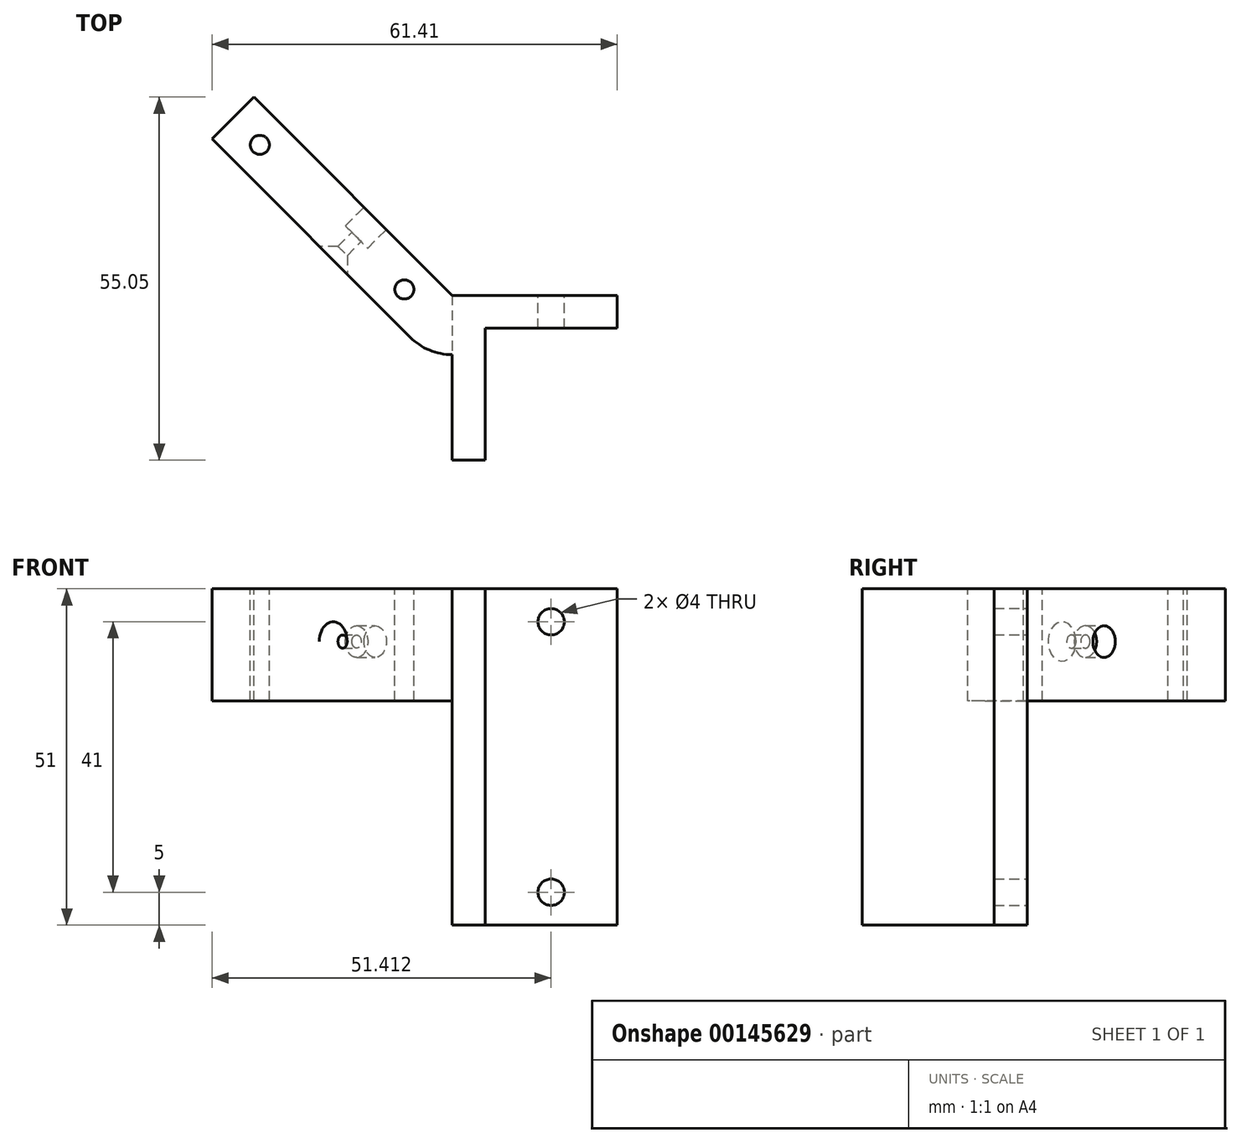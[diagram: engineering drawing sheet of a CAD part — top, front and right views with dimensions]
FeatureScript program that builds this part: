
annotation { "Feature Type Name" : "Feature", "Feature Type Description" : "" }
export const myFeature = defineFeature(function(context is Context, id is Id, definition is map)
    precondition{}
    {
        {
            var Q0;
            Q0=qCreatedBy(makeId("Top.planeOp"),FACE);
            var sketch = newSketch(context, id + "F0", { "sketchPlane" : qUnion([Q0])});
            skLineSegment(sketch, "E0", {"start": v(0.11, 9.4) * mm, "end": v(0.11, 0.4) * mm});
            skLineSegment(sketch, "E1", {"start": v(0.11, 0.4) * mm, "end": v(0.11, -15.6) * mm});
            skLineSegment(sketch, "E2", {"start": v(0.11, -15.6) * mm, "end": v(5.11, -15.6) * mm});
            skLineSegment(sketch, "E3", {"start": v(5.11, -15.6) * mm, "end": v(5.11, 4.4) * mm});
            skLineSegment(sketch, "E4", {"start": v(5.11, 4.4) * mm, "end": v(25.11, 4.4) * mm});
            skLineSegment(sketch, "E5", {"start": v(25.11, 9.4) * mm, "end": v(0.11, 9.4) * mm});
            skLineSegment(sketch, "E6", {"start": v(-29.94, 39.46) * mm, "end": v(0.11, 9.4) * mm});
            skLineSegment(sketch, "E7", {"start": v(0.11, 9.4) * mm, "end": v(-6.25, 3.04) * mm});
            skLineSegment(sketch, "E8", {"start": v(-6.25, 3.04) * mm, "end": v(-36.3, 33.1) * mm});
            skLineSegment(sketch, "E9", {"start": v(-36.3, 33.1) * mm, "end": v(-29.94, 39.46) * mm});
            skLineSegment(sketch, "E10", {"start": v(-33.12, 36.28) * mm, "end": v(-29.06, 32.2) * mm, "construction": true});
            skLineSegment(sketch, "E11", {"start": v(-29.06, 32.2) * mm, "end": v(-7.14, 10.29) * mm, "construction": true});
            skLineSegment(sketch, "E12", {"start": v(-7.14, 10.29) * mm, "end": v(-3.07, 6.22) * mm, "construction": true});
            skCircle(sketch, "E13", {"center": v(-29.06, 32.2) * mm, "radius": 1.45 * mm});
            skCircle(sketch, "E14", {"center": v(-7.14, 10.29) * mm, "radius": 1.45 * mm});
            skCircle(sketch, "E15", {"center": v(0.11, 9.4) * mm, "radius": 9 * mm});
            skLineSegment(sketch, "E16", {"start": v(25.11, 9.4) * mm, "end": v(25.11, 4.4) * mm});
            skSolve(sketch);
        }
        {
            var Q0;
            {var subQ1=sQuery(id+"F0.wireOp",EDGE,"E8");Q0=makeQuery(id+"F0.imprint","IMPRINT",FACE,{"disambiguationData":[TD([[makeQuery(id+"F0.imprint","IMPRINT",EDGE,{"derivedFrom":subQ1}),-1.0]])]});}
            var Q1;
            {var subQ0=sQuery(id+"F0.wireOp",EDGE,"E7");Q1=makeQuery(id+"F0.imprint","IMPRINT",FACE,{"disambiguationData":[TD([[makeQuery(id+"F0.imprint","IMPRINT",EDGE,{"derivedFrom":subQ0}),-1.0]])]});}
            var Q2;
            {var subQ0=sQuery(id+"F0.wireOp",EDGE,"E0");Q2=makeQuery(id+"F0.imprint","IMPRINT",FACE,{"disambiguationData":[TD([[makeQuery(id+"F0.imprint","IMPRINT",EDGE,{"derivedFrom":subQ0}),-1.0]])]});}
            var Q3;
            {var subQ4=sQuery(id+"F0.wireOp",EDGE,"kEGB38dB-wI6o-vp5B-2OdH-hbcTewE5rvnv");Q3=makeQuery(id+"F0.imprint","IMPRINT",FACE,{"disambiguationData":[TD([[makeQuery(id+"F0.imprint","IMPRINT",EDGE,{"derivedFrom":subQ4}),1.0]])]});}
            extrude(context, id + "F1", {"entities" : qUnion([Q0, Q1, Q2, Q3]), "oppositeDirection" : true, "depth" : 17 * mm});
        }
        {
            var Q0;
            {var subQ0=sQuery(id+"F0.wireOp",EDGE,"E1");Q0=makeQuery(id+"F0.imprint","IMPRINT",FACE,{"disambiguationData":[TD([[makeQuery(id+"F0.imprint","IMPRINT",EDGE,{"derivedFrom":subQ0}),1.0]])]});}
            var Q1;
            {var subQ1=sQuery(id+"F0.wireOp",EDGE,"E0");Q1=makeQuery(id+"F0.imprint","IMPRINT",FACE,{"disambiguationData":[TD([[makeQuery(id+"F0.imprint","IMPRINT",EDGE,{"derivedFrom":subQ1}),1.0]])]});}
            var Q2;
            {var subQ4=sQuery(id+"F0.wireOp",EDGE,"kEGB38dB-wI6o-vp5B-2OdH-hbcTewE5rvnv");Q2=makeQuery(id+"F0.imprint","IMPRINT",FACE,{"disambiguationData":[TD([[makeQuery(id+"F0.imprint","IMPRINT",EDGE,{"derivedFrom":subQ4}),1.0]])]});}
            var Q3;
            {var subQ0=sQuery(id+"F0.wireOp",EDGE,"E16");Q3=makeQuery(id+"F0.imprint","IMPRINT",FACE,{"disambiguationData":[TD([[makeQuery(id+"F0.imprint","IMPRINT",EDGE,{"derivedFrom":subQ0}),-1.0]])]});}
            extrude(context, id + "F2", {"entities" : qUnion([Q0, Q1, Q2, Q3]), "operationType" : NewBodyOperationType.ADD, "oppositeDirection" : true, "depth" : (17 + 34) * mm});
        }
        {
            var Q0;
            Q0=makeQuery(id+"F1.opExtrude","SWEPT_FACE",FACE,{"disambiguationData":[OSD([sQuery(id+"F0.wireOp",EDGE,"E6")])]});
            var sketch = newSketch(context, id + "F3", { "sketchPlane" : qUnion([Q0])});
            skLineSegment(sketch, "E17", {"start": v(23.07, 0) * mm, "end": v(23.07, -17) * mm, "construction": true});
            skLineSegment(sketch, "E18", {"start": v(49.07, -8) * mm, "end": v(6.57, -8) * mm, "construction": true});
            skPoint(sketch, "E19", {"position": v(23.07, -8) * mm});
            skCircle(sketch, "E20", {"center": v(23.07, -8) * mm, "radius": 2.4 * mm});
            skCircle(sketch, "E21", {"center": v(23.07, -8) * mm, "radius": 1 * mm});
            skSolve(sketch);
        }
        {
            var Q0;
            Q0=makeQuery(id+"F3.imprint","IMPRINT",FACE,{"disambiguationData":[TD([[makeQuery(id+"F3.imprint","IMPRINT",EDGE,{"derivedFrom":sQuery(id+"F3.wireOp",EDGE,"E21")}),1.0]])]});
            extrude(context, id + "F4", {"entities" : qUnion([Q0]), "operationType" : NewBodyOperationType.REMOVE, "endBound" : BoundingType.THROUGH_ALL, "oppositeDirection" : true, "depth" : 25 * mm});
        }
        {
            var Q0;
            Q0=makeQuery(id+"F3.imprint","IMPRINT",FACE,{"disambiguationData":[TD([[makeQuery(id+"F3.imprint","IMPRINT",EDGE,{"derivedFrom":sQuery(id+"F3.wireOp",EDGE,"E20")}),1.0]])]});
            extrude(context, id + "F5", {"entities" : qUnion([Q0]), "operationType" : NewBodyOperationType.REMOVE, "oppositeDirection" : true, "depth" : 4 * mm});
        }
        {
            var Q0;
            Q0=makeQuery(id+"F4.boolean.opBoolean","INTERSECT",EDGE,{"derivedFrom":[makeQuery(id+"F1.opExtrude","SWEPT_FACE",FACE,{"disambiguationData":[OSD([sQuery(id+"F0.wireOp",EDGE,"E8")])]}),makeQuery(id+"F4.opExtrude","SWEPT_FACE",FACE,{"disambiguationData":[OSD([sQuery(id+"F3.wireOp",EDGE,"E21")])]})]});
            chamfer(context, id + "F6", {"entities" : qUnion([Q0]), "width" : 2 * mm, "tangentPropagation" : true});
        }
        {
            var Q0;
            Q0=makeQuery(id+"F2.opExtrude","SWEPT_FACE",FACE,{"disambiguationData":[OSD([sQuery(id+"F0.wireOp",EDGE,"E5")])]});
            var sketch = newSketch(context, id + "F7", { "sketchPlane" : qUnion([Q0])});
            skCircle(sketch, "E22", {"center": v(-15.11, -5) * mm, "radius": 2 * mm});
            skCircle(sketch, "E23", {"center": v(-15.11, -46) * mm, "radius": 2 * mm});
            skLineSegment(sketch, "E24.0", {"start": v(-25.11, -51) * mm, "end": v(-25.11, 0) * mm});
            skLineSegment(sketch, "E25.0", {"start": v(-25.11, 0) * mm, "end": v(-0.11, 0) * mm});
            skLineSegment(sketch, "E26.0", {"start": v(-0.11, -51) * mm, "end": v(-0.11, -17) * mm});
            skLineSegment(sketch, "E27.0", {"start": v(-0.11, -17) * mm, "end": v(-0.11, 0) * mm});
            skLineSegment(sketch, "E28.0", {"start": v(-25.11, -51) * mm, "end": v(-0.11, -51) * mm});
            skSolve(sketch);
        }
        {
            var Q0;
            Q0=makeQuery(id+"F7.imprint","IMPRINT",FACE,{"disambiguationData":[TD([[makeQuery(id+"F7.imprint","IMPRINT",EDGE,{"derivedFrom":sQuery(id+"F7.wireOp",EDGE,"E22")}),1.0]])]});
            var Q1;
            Q1=makeQuery(id+"F7.imprint","IMPRINT",FACE,{"disambiguationData":[TD([[makeQuery(id+"F7.imprint","IMPRINT",EDGE,{"derivedFrom":sQuery(id+"F7.wireOp",EDGE,"E23")}),1.0]])]});
            extrude(context, id + "F8", {"entities" : qUnion([Q0, Q1]), "operationType" : NewBodyOperationType.REMOVE, "endBound" : BoundingType.THROUGH_ALL, "oppositeDirection" : true, "depth" : 25 * mm});
        }
    });
